# Revit family: VRW-3591
name_source: partatom
category: Lighting Fixtures
units: mm (PartAtom-declared; Revit-internal decimal feet)

## family parameters
Always vertical = Yes
Cut with Voids When Loaded = No
Host = Wall
Light Source = Yes
OmniClass Number = 23.80.70.00
OmniClass Title = Lighting
Part Type = Normal
Room Calculation Point = No
Round Connector Dimension = Use Diameter
Shared = No

## types (2) — shared parameters
Assembly Code = D5020200
Color Filter = 16777215
Description = LED Vandal Resistant Wall Mount
Dimming Lamp Color Temperature Shift = <None>
Emit from Line Length = 4' - 2 21/32"
Housing Finish = Metal - Viscor - White
Lamp = LED
Length = 4' - 2 21/32"
Lens Finish = Polycarbonate - Viscor - Clear
Manufacturer = CERTOLUX by VISCOR
Model = VRW-3591
Tilt Angle = -180.00°
URL = https://viscor.com
Voltage = 120 V
Width = 0' - 10 1/2"

## per-type parameters (varying)
| type | Apparent Load | Lamp Wattage | Photometric Web File |
| VRW-3591-48-LED840K40LUNV-P48P13 | 36 VA | 36 VA | VRW-3591-48-LED840K40LUNV-P48P13.ies |
| VRW-3591-48-LED840K50LUNV-P48P13 | 44 VA | 44 VA | VRW-3591-48-LED840K50LUNV-P48P13.ies |

## geometry (parser evidence)
native form markers: Sweep x1
no freeform markers — native parametric forms only
